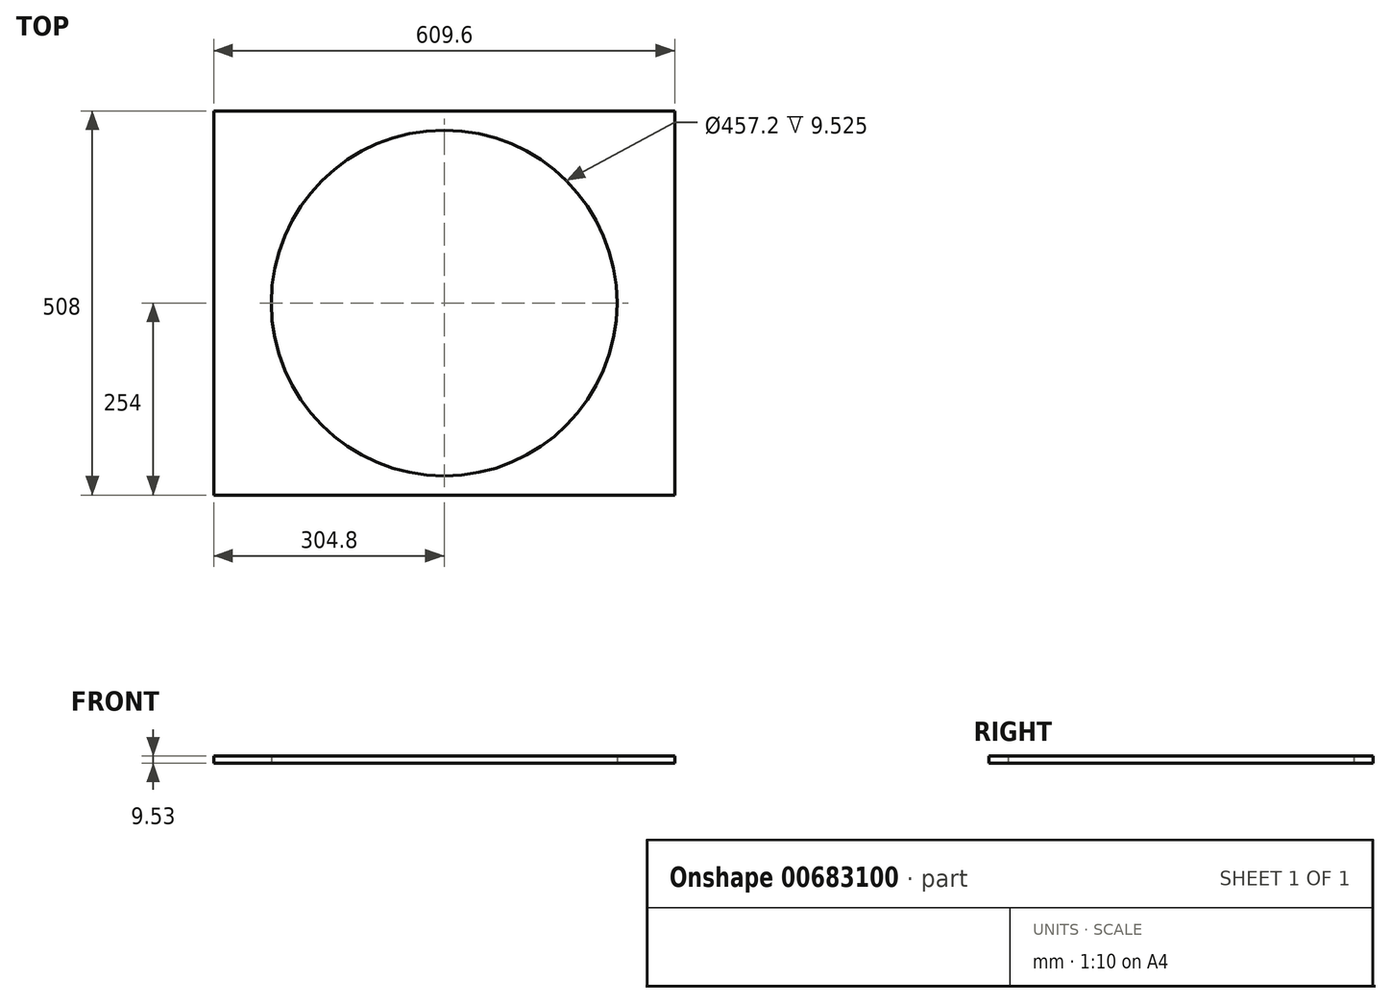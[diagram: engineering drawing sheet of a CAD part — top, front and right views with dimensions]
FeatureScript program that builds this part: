
annotation { "Feature Type Name" : "Feature", "Feature Type Description" : "" }
export const myFeature = defineFeature(function(context is Context, id is Id, definition is map)
    precondition{}
    {
        {
            var Q0;
            Q0=qCreatedBy(makeId("Top.planeOp"),FACE);
            var sketch = newSketch(context, id + "F0", { "sketchPlane" : qUnion([Q0])});
            skLineSegment(sketch, "E0.bottom", {"start": v(304.8, -254) * mm, "end": v(-304.8, -254) * mm});
            skLineSegment(sketch, "E0.top", {"start": v(304.8, 254) * mm, "end": v(-304.8, 254) * mm});
            skLineSegment(sketch, "E0.left", {"start": v(304.8, -254) * mm, "end": v(304.8, 254) * mm});
            skLineSegment(sketch, "E0.right", {"start": v(-304.8, -254) * mm, "end": v(-304.8, 254) * mm});
            skPoint(sketch, "E0.middle", {"position": v(0, 0) * mm});
            skCircle(sketch, "E1", {"center": v(0, 0) * mm, "radius": 228.6 * mm});
            skSolve(sketch);
        }
        {
            var Q0;
            Q0 = qSketchRegion(id + "F0", true);
            var Q1;
            Q1=makeQuery(id+"F0.imprint","IMPRINT",FACE,{"disambiguationData":[TD([[makeQuery(id+"F0.imprint","IMPRINT",EDGE,{"derivedFrom":sQuery(id+"F0.wireOp",EDGE,"E0.bottom")}),-1.0]])]});
            extrude(context, id + "F1", {"entities" : qUnion([Q0, Q1]), "depth" : 9.52 * mm, "offsetDistance" : 25.4 * mm});
        }
    });
